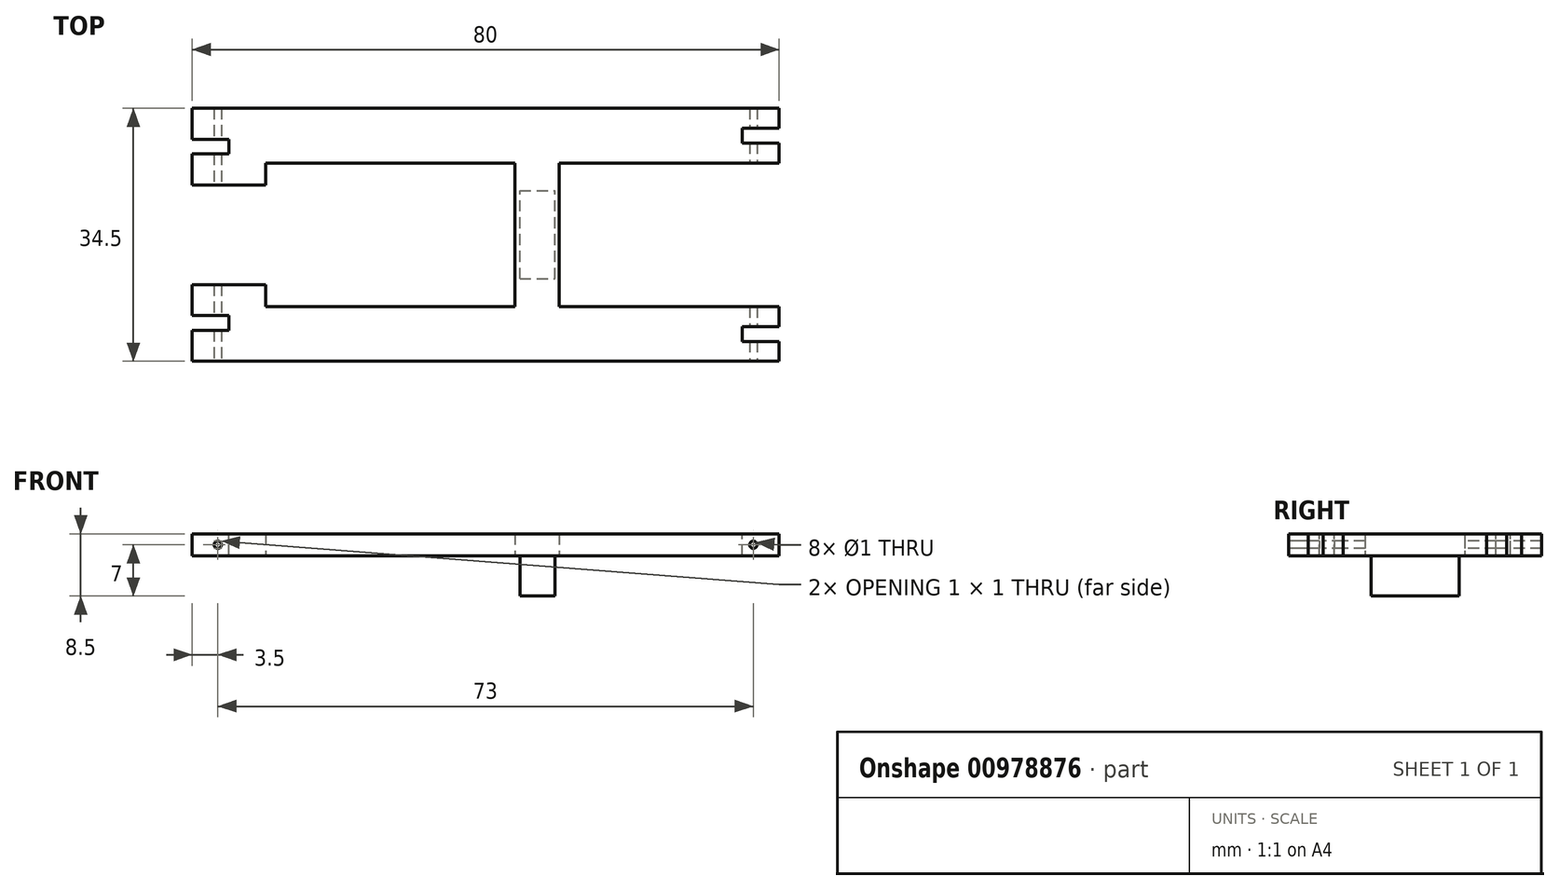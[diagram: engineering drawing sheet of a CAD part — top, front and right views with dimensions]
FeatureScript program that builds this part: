
annotation { "Feature Type Name" : "Feature", "Feature Type Description" : "" }
export const myFeature = defineFeature(function(context is Context, id is Id, definition is map)
    precondition{}
    {
        {
            var Q0;
            Q0=qCreatedBy(makeId("Top.planeOp"),FACE);
            var sketch = newSketch(context, id + "F0", { "sketchPlane" : qUnion([Q0])});
            skLineSegment(sketch, "E0.bottom", {"start": v(-25, 17.25) * mm, "end": v(25, 17.25) * mm});
            skLineSegment(sketch, "E0.top", {"start": v(-25, -17.25) * mm, "end": v(25, -17.25) * mm});
            skLineSegment(sketch, "E0.left", {"start": v(-25, 17.25) * mm, "end": v(-25, -17.25) * mm});
            skLineSegment(sketch, "E0.right", {"start": v(25, 17.25) * mm, "end": v(25, -17.25) * mm});
            skPoint(sketch, "E0.middle", {"position": v(0, 0) * mm});
            skLineSegment(sketch, "E1", {"start": v(-15, 17.25) * mm, "end": v(-15, -17.25) * mm});
            skLineSegment(sketch, "E2", {"start": v(-25, 6.8) * mm, "end": v(-15, 6.8) * mm});
            skLineSegment(sketch, "E3", {"start": v(-25, -6.8) * mm, "end": v(-15, -6.8) * mm});
            skLineSegment(sketch, "E4", {"start": v(-15, 9.8) * mm, "end": v(25, 9.8) * mm});
            skLineSegment(sketch, "E5", {"start": v(-15, -9.8) * mm, "end": v(25, -9.8) * mm});
            skLineSegment(sketch, "E6", {"start": v(19, 17.25) * mm, "end": v(19, -17.25) * mm});
            skLineSegment(sketch, "E7", {"start": v(19, 6) * mm, "end": v(25, 6) * mm});
            skLineSegment(sketch, "E8", {"start": v(19, -6) * mm, "end": v(25, -6) * mm});
            skLineSegment(sketch, "E9.bottom", {"start": v(24.44, -6) * mm, "end": v(19.69, -6) * mm});
            skLineSegment(sketch, "E9.top", {"start": v(24.44, 6) * mm, "end": v(19.69, 6) * mm});
            skLineSegment(sketch, "E9.left", {"start": v(24.44, -6) * mm, "end": v(24.44, 6) * mm});
            skLineSegment(sketch, "E9.right", {"start": v(19.69, -6) * mm, "end": v(19.69, 6) * mm});
            skLineSegment(sketch, "E10.bottom", {"start": v(25, -17.25) * mm, "end": v(55, -17.25) * mm});
            skLineSegment(sketch, "E10.top", {"start": v(25, -9.8) * mm, "end": v(55, -9.8) * mm});
            skLineSegment(sketch, "E10.left", {"start": v(25, -17.25) * mm, "end": v(25, -9.8) * mm});
            skLineSegment(sketch, "E10.right", {"start": v(55, -17.25) * mm, "end": v(55, -9.8) * mm});
            skLineSegment(sketch, "E11.bottom", {"start": v(25, 17.25) * mm, "end": v(55, 17.25) * mm});
            skLineSegment(sketch, "E11.top", {"start": v(25, 9.8) * mm, "end": v(55, 9.8) * mm});
            skLineSegment(sketch, "E11.left", {"start": v(25, 17.25) * mm, "end": v(25, 9.8) * mm});
            skLineSegment(sketch, "E11.right", {"start": v(55, 17.25) * mm, "end": v(55, 9.8) * mm});
            skSolve(sketch);
        }
        {
            var Q0;
            {var subQ0=sQuery(id+"F0.wireOp",EDGE,"E11.bottom");Q0=makeQuery(id+"F0.imprint","IMPRINT",FACE,{"disambiguationData":[TD([[makeQuery(id+"F0.imprint","IMPRINT",EDGE,{"derivedFrom":subQ0}),-1.0]])]});}
            var Q1;
            {var subQ0=sQuery(id+"F0.wireOp",EDGE,"E10.bottom");Q1=makeQuery(id+"F0.imprint","IMPRINT",FACE,{"disambiguationData":[TD([[makeQuery(id+"F0.imprint","IMPRINT",EDGE,{"derivedFrom":subQ0}),1.0]])]});}
            var Q2;
            {var subQ3=sQuery(id+"F0.wireOp",EDGE,"E6");var subQ5=sQuery(id+"F0.wireOp",EDGE,"E5");var subQ7=makeQuery(id+"F0.imprint","INTERSECT",VERTEX,{"derivedFrom":[subQ5,subQ3]});Q2=makeQuery(id+"F0.imprint","IMPRINT",FACE,{"disambiguationData":[TD([[makeQuery(id+"F0.imprint","IMPRINT",EDGE,{"disambiguationData":[TD([[subQ7,-1.0]])],"derivedFrom":subQ3}),1.0]])]});}
            var Q3;
            {var subQ3=sQuery(id+"F0.wireOp",EDGE,"E6");var subQ4=sQuery(id+"F0.wireOp",EDGE,"E5");var subQ5=makeQuery(id+"F0.imprint","INTERSECT",VERTEX,{"derivedFrom":[subQ4,subQ3]});Q3=makeQuery(id+"F0.imprint","IMPRINT",FACE,{"disambiguationData":[TD([[makeQuery(id+"F0.imprint","IMPRINT",EDGE,{"disambiguationData":[TD([[subQ5,1.0]])],"derivedFrom":subQ3}),1.0]])]});}
            var Q4;
            {var subQ2=sQuery(id+"F0.wireOp",EDGE,"E9.left");Q4=makeQuery(id+"F0.imprint","IMPRINT",FACE,{"disambiguationData":[TD([[makeQuery(id+"F0.imprint","IMPRINT",EDGE,{"derivedFrom":subQ2}),1.0]])]});}
            var Q5;
            {var subQ5=sQuery(id+"F0.wireOp",EDGE,"E9.right");Q5=makeQuery(id+"F0.imprint","IMPRINT",FACE,{"disambiguationData":[TD([[makeQuery(id+"F0.imprint","IMPRINT",EDGE,{"derivedFrom":subQ5}),1.0]])]});}
            var Q6;
            {var subQ5=sQuery(id+"F0.wireOp",EDGE,"E9.left");Q6=makeQuery(id+"F0.imprint","IMPRINT",FACE,{"disambiguationData":[TD([[makeQuery(id+"F0.imprint","IMPRINT",EDGE,{"derivedFrom":subQ5}),-1.0]])]});}
            var Q7;
            {var subQ0=sQuery(id+"F0.wireOp",EDGE,"E7");var subQ6=sQuery(id+"F0.wireOp",EDGE,"E6");var subQ8=makeQuery(id+"F0.imprint","INTERSECT",VERTEX,{"derivedFrom":[subQ6,subQ0]});Q7=makeQuery(id+"F0.imprint","IMPRINT",FACE,{"disambiguationData":[TD([[makeQuery(id+"F0.imprint","IMPRINT",EDGE,{"disambiguationData":[TD([[subQ8,1.0]])],"derivedFrom":subQ6}),1.0]])]});}
            var Q8;
            {var subQ1=sQuery(id+"F0.wireOp",EDGE,"E0.bottom");var subQ3=sQuery(id+"F0.wireOp",EDGE,"E6");var subQ4=makeQuery(id+"F0.imprint","INTERSECT",VERTEX,{"derivedFrom":[subQ1,subQ3]});Q8=makeQuery(id+"F0.imprint","IMPRINT",FACE,{"disambiguationData":[TD([[makeQuery(id+"F0.imprint","IMPRINT",EDGE,{"disambiguationData":[TD([[subQ4,-1.0]])],"derivedFrom":subQ3}),1.0]])]});}
            var Q9;
            {var subQ0=sQuery(id+"F0.wireOp",EDGE,"E1");var subQ1=sQuery(id+"F0.wireOp",EDGE,"E0.bottom");var subQ2=makeQuery(id+"F0.imprint","INTERSECT",VERTEX,{"derivedFrom":[subQ1,subQ0]});Q9=makeQuery(id+"F0.imprint","IMPRINT",FACE,{"disambiguationData":[TD([[makeQuery(id+"F0.imprint","IMPRINT",EDGE,{"disambiguationData":[TD([[subQ2,-1.0]])],"derivedFrom":subQ1}),-1.0]])]});}
            var Q10;
            {var subQ0=sQuery(id+"F0.wireOp",EDGE,"E1");var subQ1=sQuery(id+"F0.wireOp",EDGE,"E0.top");var subQ2=makeQuery(id+"F0.imprint","INTERSECT",VERTEX,{"derivedFrom":[subQ1,subQ0]});Q10=makeQuery(id+"F0.imprint","IMPRINT",FACE,{"disambiguationData":[TD([[makeQuery(id+"F0.imprint","IMPRINT",EDGE,{"disambiguationData":[TD([[subQ2,-1.0]])],"derivedFrom":subQ1}),1.0]])]});}
            var Q11;
            {var subQ6=sQuery(id+"F0.wireOp",EDGE,"E3");Q11=makeQuery(id+"F0.imprint","IMPRINT",FACE,{"disambiguationData":[TD([[makeQuery(id+"F0.imprint","IMPRINT",EDGE,{"derivedFrom":subQ6}),-1.0]])]});}
            var Q12;
            {var subQ0=sQuery(id+"F0.wireOp",EDGE,"E2");Q12=makeQuery(id+"F0.imprint","IMPRINT",FACE,{"disambiguationData":[TD([[makeQuery(id+"F0.imprint","IMPRINT",EDGE,{"derivedFrom":subQ0}),1.0]])]});}
            extrude(context, id + "F1", {"entities" : qUnion([Q0, Q1, Q2, Q3, Q4, Q5, Q6, Q7, Q8, Q9, Q10, Q11, Q12]), "depth" : 3 * mm, "offsetDistance" : 25 * mm});
        }
        {
            var Q0;
            {var subQ2=sQuery(id+"F0.wireOp",EDGE,"E9.left");Q0=makeQuery(id+"F0.imprint","IMPRINT",FACE,{"disambiguationData":[TD([[makeQuery(id+"F0.imprint","IMPRINT",EDGE,{"derivedFrom":subQ2}),1.0]])]});}
            extrude(context, id + "F2", {"entities" : qUnion([Q0]), "operationType" : NewBodyOperationType.ADD, "oppositeDirection" : true, "depth" : 5.5 * mm, "offsetDistance" : 25 * mm});
        }
        {
            var Q0;
            Q0=makeQuery(id+"F1.opExtrude","CAP_FACE",FACE,{"disambiguationData":[OSD([sQuery(id+"F0.wireOp",EDGE,"E0.bottom"),sQuery(id+"F0.wireOp",EDGE,"E0.top"),sQuery(id+"F0.wireOp",EDGE,"E0.left"),sQuery(id+"F0.wireOp",EDGE,"E0.right"),sQuery(id+"F0.wireOp",EDGE,"E1"),sQuery(id+"F0.wireOp",EDGE,"E2"),sQuery(id+"F0.wireOp",EDGE,"E3"),sQuery(id+"F0.wireOp",EDGE,"E4"),sQuery(id+"F0.wireOp",EDGE,"E5"),sQuery(id+"F0.wireOp",EDGE,"E6"),sQuery(id+"F0.wireOp",EDGE,"E10.bottom"),sQuery(id+"F0.wireOp",EDGE,"E10.top"),sQuery(id+"F0.wireOp",EDGE,"E10.right"),sQuery(id+"F0.wireOp",EDGE,"E11.bottom"),sQuery(id+"F0.wireOp",EDGE,"E11.top"),sQuery(id+"F0.wireOp",EDGE,"E11.right")])],"isStart":false});
            var sketch = newSketch(context, id + "F3", { "sketchPlane" : qUnion([Q0])});
            skLineSegment(sketch, "E12", {"start": v(-25, 12.03) * mm, "end": v(-15, 12.03) * mm, "construction": true});
            skPoint(sketch, "E12.endSnap0", {"position": v(-25, 12.03) * mm});
            skLineSegment(sketch, "E13", {"start": v(-25, -12.03) * mm, "end": v(-15, -12.03) * mm, "construction": true});
            skLineSegment(sketch, "E14.bottom", {"start": v(-25, 13.03) * mm, "end": v(-20, 13.03) * mm});
            skLineSegment(sketch, "E14.top", {"start": v(-25, 11.03) * mm, "end": v(-20, 11.03) * mm});
            skLineSegment(sketch, "E14.left", {"start": v(-25, 13.03) * mm, "end": v(-25, 11.03) * mm});
            skLineSegment(sketch, "E14.right", {"start": v(-20, 13.03) * mm, "end": v(-20, 11.03) * mm});
            skPoint(sketch, "E14.middle", {"position": v(-22.5, 12.03) * mm});
            skLineSegment(sketch, "E15.bottom", {"start": v(-20, -11.03) * mm, "end": v(-25, -11.03) * mm});
            skLineSegment(sketch, "E15.top", {"start": v(-20, -13.03) * mm, "end": v(-25, -13.03) * mm});
            skLineSegment(sketch, "E15.left", {"start": v(-20, -11.03) * mm, "end": v(-20, -13.03) * mm});
            skLineSegment(sketch, "E15.right", {"start": v(-25, -11.03) * mm, "end": v(-25, -13.03) * mm});
            skPoint(sketch, "E15.middle", {"position": v(-22.5, -12.03) * mm});
            skPoint(sketch, "E15.middle.positionSnap0", {"position": v(-22.5, 11.03) * mm});
            skPoint(sketch, "E15.centerSnap0", {"position": v(-22.5, 11.03) * mm});
            skSolve(sketch);
        }
        {
            var Q0;
            Q0=makeQuery(id+"F3.imprint","IMPRINT",FACE,{"disambiguationData":[TD([[makeQuery(id+"F3.imprint","IMPRINT",EDGE,{"derivedFrom":sQuery(id+"F3.wireOp",EDGE,"E14.bottom")}),-1.0]])]});
            var Q1;
            Q1=makeQuery(id+"F3.imprint","IMPRINT",FACE,{"disambiguationData":[TD([[makeQuery(id+"F3.imprint","IMPRINT",EDGE,{"derivedFrom":sQuery(id+"F3.wireOp",EDGE,"E15.bottom")}),1.0]])]});
            extrude(context, id + "F4", {"entities" : qUnion([Q0, Q1]), "operationType" : NewBodyOperationType.REMOVE, "oppositeDirection" : true, "depth" : 25 * mm, "offsetDistance" : 25 * mm});
        }
        {
            var Q0;
            Q0=makeQuery(id+"F1.opExtrude","SWEPT_FACE",FACE,{"disambiguationData":[OSD([sQuery(id+"F0.wireOp",EDGE,"E0.top"),sQuery(id+"F0.wireOp",EDGE,"E10.bottom")])]});
            var sketch = newSketch(context, id + "F5", { "sketchPlane" : qUnion([Q0])});
            skPoint(sketch, "E16", {"position": v(-21.5, 1.5) * mm});
            skPoint(sketch, "E16.positionSnap0", {"position": v(-25, 1.5) * mm});
            skPoint(sketch, "E17", {"position": v(51.5, 1.5) * mm});
            skPoint(sketch, "E17.positionSnap0", {"position": v(55, 1.5) * mm});
            skSolve(sketch);
        }
        {
            var Q0;
            Q0=sQuery(id+"F5.wireOp",VERTEX,"E16");
            var Q1;
            Q1=sQuery(id+"F5.wireOp",VERTEX,"E17");
            var Q2;
            Q2=makeQuery(id+"F1.opExtrude","SWEPT_BODY",BODY,{"disambiguationData":[OSD([sQuery(id+"F0.wireOp",EDGE,"E0.bottom"),sQuery(id+"F0.wireOp",EDGE,"E0.top"),sQuery(id+"F0.wireOp",EDGE,"E0.left"),sQuery(id+"F0.wireOp",EDGE,"E0.right"),sQuery(id+"F0.wireOp",EDGE,"E1"),sQuery(id+"F0.wireOp",EDGE,"E2"),sQuery(id+"F0.wireOp",EDGE,"E3"),sQuery(id+"F0.wireOp",EDGE,"E4"),sQuery(id+"F0.wireOp",EDGE,"E5"),sQuery(id+"F0.wireOp",EDGE,"E6"),sQuery(id+"F0.wireOp",EDGE,"E10.bottom"),sQuery(id+"F0.wireOp",EDGE,"E10.top"),sQuery(id+"F0.wireOp",EDGE,"E10.right"),sQuery(id+"F0.wireOp",EDGE,"E11.bottom"),sQuery(id+"F0.wireOp",EDGE,"E11.top"),sQuery(id+"F0.wireOp",EDGE,"E11.right")])]});
            hole(context, id + "F6", {"style" : HoleStyle.SIMPLE, "endStyle" : HoleEndStyle.THROUGH, "holeDiameter" : 1 * mm, "majorDiameter" : 5 * mm, "isTappedThrough" : true, "tappedDepth" : 12 * mm, "tapClearance" : 3, "locations" : qUnion([Q0, Q1]), "scope" : qUnion([Q2])});
        }
        {
            var Q0;
            Q0=makeQuery(id+"F1.opExtrude","CAP_FACE",FACE,{"disambiguationData":[OSD([sQuery(id+"F0.wireOp",EDGE,"E0.bottom"),sQuery(id+"F0.wireOp",EDGE,"E0.top"),sQuery(id+"F0.wireOp",EDGE,"E0.left"),sQuery(id+"F0.wireOp",EDGE,"E0.right"),sQuery(id+"F0.wireOp",EDGE,"E1"),sQuery(id+"F0.wireOp",EDGE,"E2"),sQuery(id+"F0.wireOp",EDGE,"E3"),sQuery(id+"F0.wireOp",EDGE,"E4"),sQuery(id+"F0.wireOp",EDGE,"E5"),sQuery(id+"F0.wireOp",EDGE,"E6"),sQuery(id+"F0.wireOp",EDGE,"E10.bottom"),sQuery(id+"F0.wireOp",EDGE,"E10.top"),sQuery(id+"F0.wireOp",EDGE,"E10.right"),sQuery(id+"F0.wireOp",EDGE,"E11.bottom"),sQuery(id+"F0.wireOp",EDGE,"E11.top"),sQuery(id+"F0.wireOp",EDGE,"E11.right")])],"isStart":false});
            var sketch = newSketch(context, id + "F7", { "sketchPlane" : qUnion([Q0])});
            skLineSegment(sketch, "E18.bottom", {"start": v(50, -12.52) * mm, "end": v(60, -12.52) * mm});
            skLineSegment(sketch, "E18.top", {"start": v(50, -14.52) * mm, "end": v(60, -14.52) * mm});
            skLineSegment(sketch, "E18.left", {"start": v(50, -12.52) * mm, "end": v(50, -14.52) * mm});
            skLineSegment(sketch, "E18.right", {"start": v(60, -12.52) * mm, "end": v(60, -14.52) * mm});
            skPoint(sketch, "E18.middle", {"position": v(55, -13.53) * mm});
            skLineSegment(sketch, "E19.bottom", {"start": v(50, 14.52) * mm, "end": v(60, 14.53) * mm});
            skLineSegment(sketch, "E19.top", {"start": v(50, 12.52) * mm, "end": v(60, 12.53) * mm});
            skLineSegment(sketch, "E19.left", {"start": v(50, 14.53) * mm, "end": v(50, 12.53) * mm});
            skLineSegment(sketch, "E19.right", {"start": v(60, 14.53) * mm, "end": v(60, 12.53) * mm});
            skPoint(sketch, "E19.middle", {"position": v(55, 13.53) * mm});
            skSolve(sketch);
        }
        {
            var Q0;
            Q0 = qSketchRegion(id + "F7", true);
            extrude(context, id + "F8", {"entities" : qUnion([Q0]), "operationType" : NewBodyOperationType.REMOVE, "oppositeDirection" : true, "depth" : 25 * mm, "offsetDistance" : 25 * mm});
        }
    });
